# Revit family: IS_iLifeB_T5347_BIM_GB
name_source: partatom
category: Plumbing Fixtures
units: mm (PartAtom-declared; Revit-internal decimal feet)

## family parameters
Always vertical = No
Cut with Voids When Loaded = No
OmniClass Number = 23.45.05.21.11.11
OmniClass Title = Water Operated Water Closets
Part Type = Normal
Room Calculation Point = No
Round Connector Dimension = Use Diameter
Shared = No
Work Plane-Based = No

## types (1)
- T534701 - Ideal Standard i.life B, wallhung bowl, RimLS+, hidden fixation, Easyfix+, with ablution trim mounted - White Finish
    AreaUnits = millimetres
    AssetType = Fixed
    BIMObjectName = IS_IdealStandard_WCpans_i.lifeB_T5347
    BIMobject category = Toilets
    BIMobject category code = toilets
    BIMobject main category = Sanitary
    BIMobject main category code = sanitary
    BarCode = 8014140503903
    Brand = Ideal Standard
    Brand url = http://www.idealstandard.co.uk
    Category = Sanitary
    Classification = WC Pans
    Color = White
    ConnectionType = Plumbing
    Cost = 0 $
    CurrencyUnit = £
    CurrentRevision = 1
    Date of publishing = 22/07/2022
    Description = Ideal Standard i.life B, wallhung bowl, RimLS+, hidden fixation, Easyfix+, with ablution trim mounted, white, in carton box, EU pallet
    DurationUnit = Years
    Edition number = 1
    ElementType = Fixed
    ExpectedLife = 99
    Features = wallhung bowl, RimLS+, hidden fixation, Easyfix+, with ablution trim mounted, white, in carton box, EU pallet
    Finish = White
    GTIN code = https://8014140503903
    Help = https://www.idealstandard.co.uk
    IFC Classification = Sanitary Terminal
    IfcExportAs = IfcSanitaryTerminalType
    IfcExportType = TOILETPAN
    Installation instructions = https://www.idealstandard.co.uk
    InstallationInstructions = https://www.idealstandard.co.uk
    LinearUnits = millimetres
    MainColor = White
    MaintenanceInformation = https://www.idealstandard.co.uk
    Manufacturer = Ideal Standard
    Manufacturer name = Ideal Standard
    ManufacturerURL = https://www.idealstandard.co.uk
    Material = Fireclay
    Material main = Fireclay
    Model = T534701
    ModelNumber = T534701
    ModelReference = Ideal Standard i.life B, wallhung bowl, RimLS+, hidden fixation, Easyfix+, with ablution trim mounted
    NBS Reference Code = 45-35-70/384
    NBS Reference Description = WC pans
    Name = WCpans_i.lifeB_T5347_IdealStandard
    NettWeight = 22.5
    NominalDepth = 540 mm
    NominalHeight = 337 mm
    NominalLength = 540 mm
    NominalWidth = 354 mm
    OmniClass Code = 23-31 19 00
    OmniClass Description = Toilets
    PanColor = White
    PanMaterial = Finefire Clay
    PanMounting = Wall Hung
    PredefinedType = WC Pans
    Product Guid = 18d8f11c-6dfe-4b20-8f36-c714ff56b218
    Product SKU = T5347
    Product certification = https://www.idealstandard.co.uk
    Product data url = https://bimobject.com
    Product family = I.Life B
    Product group = Sanitary
    Product name = I.Life b, wallhung bowl, Easyfix+
    Product url = https://www.idealstandard.co.uk
    ProductInformation = https://www.idealstandard.co.uk
    QR code = http://bimobject.com
    SeatColor = White
    SeatHasCover = No
    SeatMaterial = Acrylic
    Shape = sculptured
    Size = 355 x 540 x 337 mm
    Space = Internal
    SpareParts = https://www.idealstandard.co.uk
    Technical description = https://www.idealstandard.co.uk
    ToiletPanType = Wall -Hung WC Bowl
    ToiletType = Wall -Hung WC Bowl
    UNSPSC Code = 301815
    URL = https://www.idealstandard.co.uk
    Uniclass 2015 Code = Pr_40_20_93_94
    Uniclass 2015 Name = WC pans
    Uniclass2015Code = Pr_40_20_93_94
    Uniclass2015Title = WC pans
    Uniclass2015Version = v1.26
    Version = 1
    VolumeUnits = Liters
    WRASURL = https://www.wrasapprovals.co.uk
    WarrantyDescription = manufacturer warranty
    WarrantyDurationUnit = Years
    Weight Net (Kg) = 22.5
    Youtube clip = https://www.youtube.com

## geometry (parser evidence)
native form markers: Sweep x2
no freeform markers — native parametric forms only
